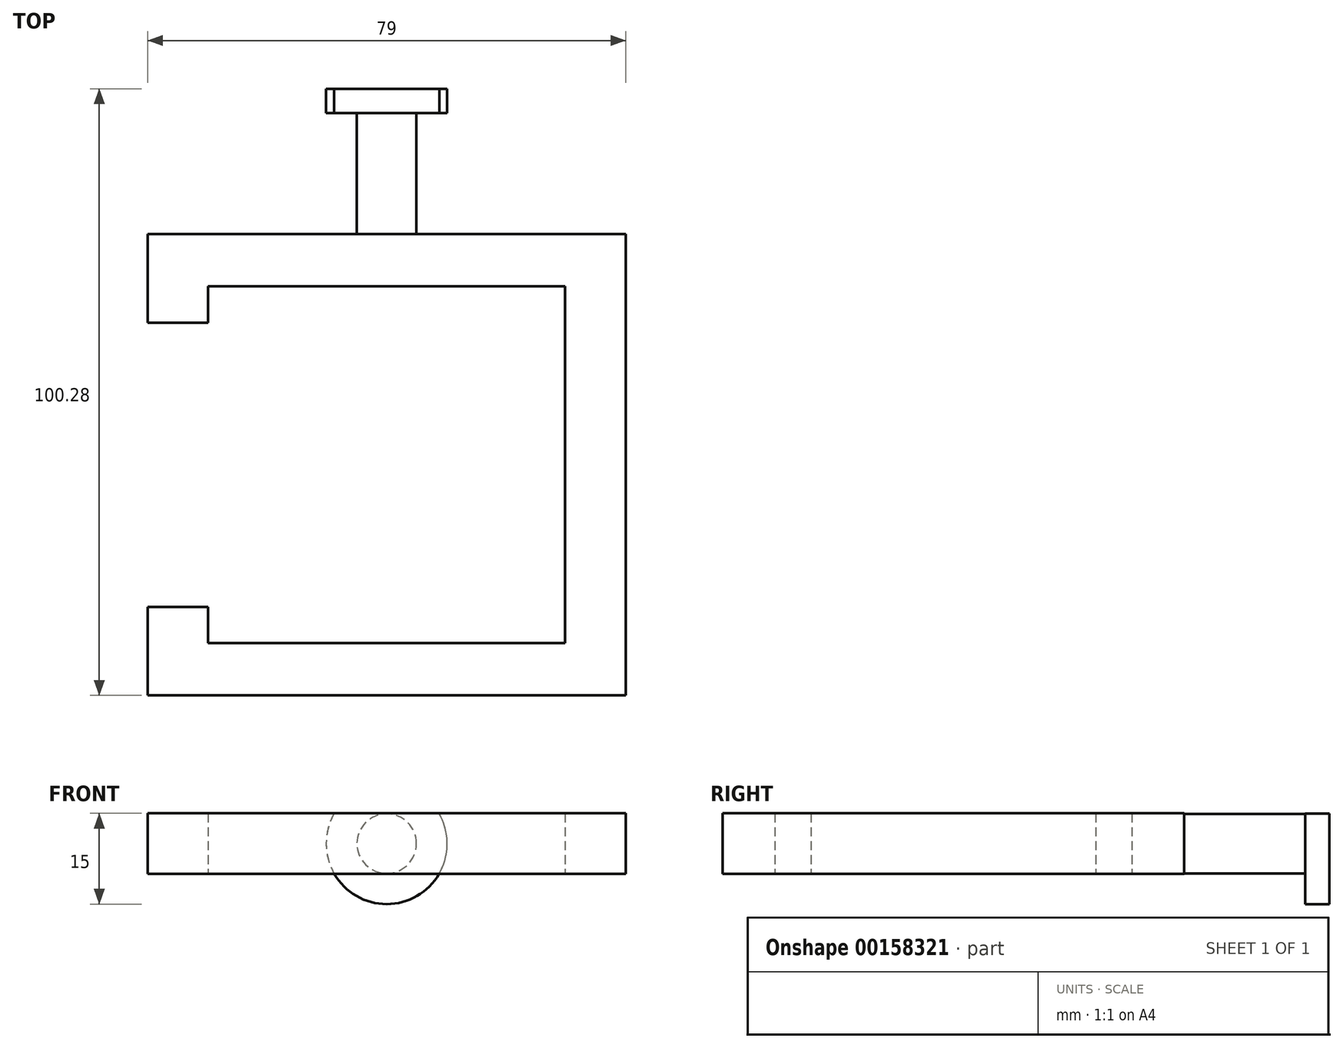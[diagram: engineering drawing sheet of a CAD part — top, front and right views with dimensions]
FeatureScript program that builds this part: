
annotation { "Feature Type Name" : "Feature", "Feature Type Description" : "" }
export const myFeature = defineFeature(function(context is Context, id is Id, definition is map)
    precondition{}
    {
        {
            var Q0;
            Q0=qCreatedBy(makeId("Top.planeOp"),FACE);
            var sketch = newSketch(context, id + "F0", { "sketchPlane" : qUnion([Q0])});
            skLineSegment(sketch, "E0.bottom", {"start": v(-29.5, -29.5) * mm, "end": v(29.5, -29.5) * mm});
            skLineSegment(sketch, "E0.top", {"start": v(-29.5, 29.5) * mm, "end": v(29.5, 29.5) * mm});
            skLineSegment(sketch, "E0.left", {"start": v(-29.5, -29.5) * mm, "end": v(-29.5, 29.5) * mm});
            skLineSegment(sketch, "E0.right", {"start": v(29.5, -29.5) * mm, "end": v(29.5, 29.5) * mm});
            skPoint(sketch, "E0.middle", {"position": v(0, 0) * mm});
            skLineSegment(sketch, "E1.bottom", {"start": v(-39.5, 38.14) * mm, "end": v(39.5, 38.14) * mm});
            skLineSegment(sketch, "E1.top", {"start": v(-39.5, -38.14) * mm, "end": v(39.5, -38.14) * mm});
            skLineSegment(sketch, "E1.left", {"start": v(-39.5, 38.14) * mm, "end": v(-39.5, -38.14) * mm});
            skLineSegment(sketch, "E1.right", {"start": v(39.5, 38.14) * mm, "end": v(39.5, -38.14) * mm});
            skLineSegment(sketch, "E2", {"start": v(-39.5, 23.5) * mm, "end": v(-29.5, 23.5) * mm});
            skLineSegment(sketch, "E3", {"start": v(-29.5, 23.5) * mm, "end": v(-29.5, 29.5) * mm});
            skLineSegment(sketch, "E4", {"start": v(-29.5, -29.5) * mm, "end": v(-39.5, -29.5) * mm});
            skLineSegment(sketch, "E5", {"start": v(-39.5, -23.5) * mm, "end": v(-29.5, -23.5) * mm});
            skLineSegment(sketch, "E6", {"start": v(-29.5, -23.5) * mm, "end": v(-29.5, -29.5) * mm});
            skSolve(sketch);
        }
        {
            var Q0;
            Q0=makeQuery(id+"F0.imprint","IMPRINT",FACE,{"disambiguationData":[TD([[makeQuery(id+"F0.imprint","IMPRINT",EDGE,{"derivedFrom":sQuery(id+"F0.wireOp",EDGE,"E0.bottom")}),-1.0]])]});
            var Q1;
            {var subQ0=sQuery(id+"F0.wireOp",EDGE,"E4");Q1=makeQuery(id+"F0.imprint","IMPRINT",FACE,{"disambiguationData":[TD([[makeQuery(id+"F0.imprint","IMPRINT",EDGE,{"derivedFrom":subQ0}),-1.0]])]});}
            extrude(context, id + "F1", {"entities" : qUnion([Q0, Q1]), "endBound" : BoundingType.SYMMETRIC, "depth" : 10 * mm});
        }
        {
            var Q0;
            Q0=makeQuery(id+"F1.opExtrude","SWEPT_FACE",FACE,{"disambiguationData":[OSD([sQuery(id+"F0.wireOp",EDGE,"E1.bottom")])]});
            var sketch = newSketch(context, id + "F2", { "sketchPlane" : qUnion([Q0])});
            skCircle(sketch, "E7", {"center": v(0, 0) * mm, "radius": 4.92 * mm});
            skSolve(sketch);
        }
        {
            var Q0;
            Q0=makeQuery(id+"F2.imprint","IMPRINT",FACE,{"disambiguationData":[TD([[makeQuery(id+"F2.imprint","IMPRINT",EDGE,{"derivedFrom":sQuery(id+"F2.wireOp",EDGE,"E7")}),1.0]])]});
            extrude(context, id + "F3", {"entities" : qUnion([Q0]), "operationType" : NewBodyOperationType.ADD, "depth" : 20 * mm});
        }
        {
            var Q0;
            Q0=makeQuery(id+"F3.opExtrude","CAP_FACE",FACE,{"disambiguationData":[OSD([sQuery(id+"F2.wireOp",EDGE,"E7")])],"isStart":false});
            var sketch = newSketch(context, id + "F4", { "sketchPlane" : qUnion([Q0])});
            skCircle(sketch, "E8", {"center": v(0, 0) * mm, "radius": 10 * mm});
            skLineSegment(sketch, "E9", {"start": v(8.68, 4.97) * mm, "end": v(-8.68, 4.97) * mm});
            skSolve(sketch);
        }
        {
            var Q0;
            Q0=makeQuery(id+"F4.imprint","IMPRINT",FACE,{"disambiguationData":[TD([[makeQuery(id+"F4.imprint","IMPRINT",EDGE,{"derivedFrom":makeQuery(id+"F3.opExtrude","CAP_EDGE",EDGE,{"disambiguationData":[OSD([sQuery(id+"F2.wireOp",EDGE,"E7")])],"isStart":false})}),1.0]])]});
            var Q1;
            {var subQ0=sQuery(id+"F4.wireOp",EDGE,"E9");Q1=makeQuery(id+"F4.imprint","IMPRINT",FACE,{"disambiguationData":[TD([[makeQuery(id+"F4.imprint","IMPRINT",EDGE,{"derivedFrom":subQ0}),1.0]])]});}
            extrude(context, id + "F5", {"entities" : qUnion([Q0, Q1]), "operationType" : NewBodyOperationType.ADD, "depth" : 4 * mm});
        }
    });
